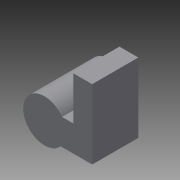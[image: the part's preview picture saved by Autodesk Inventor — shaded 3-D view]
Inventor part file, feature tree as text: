
AUTODESK INVENTOR PART (.ipt)
format: ipt  version: 2015 (Build 190159000, 159)  size: 105,472 bytes
history: native  units: in
note: dims shown in document units (in); Inventor stores cm internally (conversion verified against a paired STEP export)
features: extrude x2, sketch x2, reference x1
ambient origin geometry x8: Origin, YZ Plane, XZ Plane, XY Plane, X Axis, Y Axis, Z Axis, Center Point
bodies: Solid1 (feature_tree)
feature tree (5):
  extrude  "Extrusion1"  Depth=0.9375in TaperAngle=0.0deg
  extrude  "Extrusion2"  [1 undecoded]
  sketch  "Sketch1"  dims[d0=0.375in d1=0.0in d2=0.9375in d3=0.0in]
  reference  "Reference1"
  sketch  "Sketch2"
note: 1 required parameter value undecoded (feature->parameter linkage not recoverable at this tier; creation-order binding heuristic only, values carry confidence <= 0.55)
